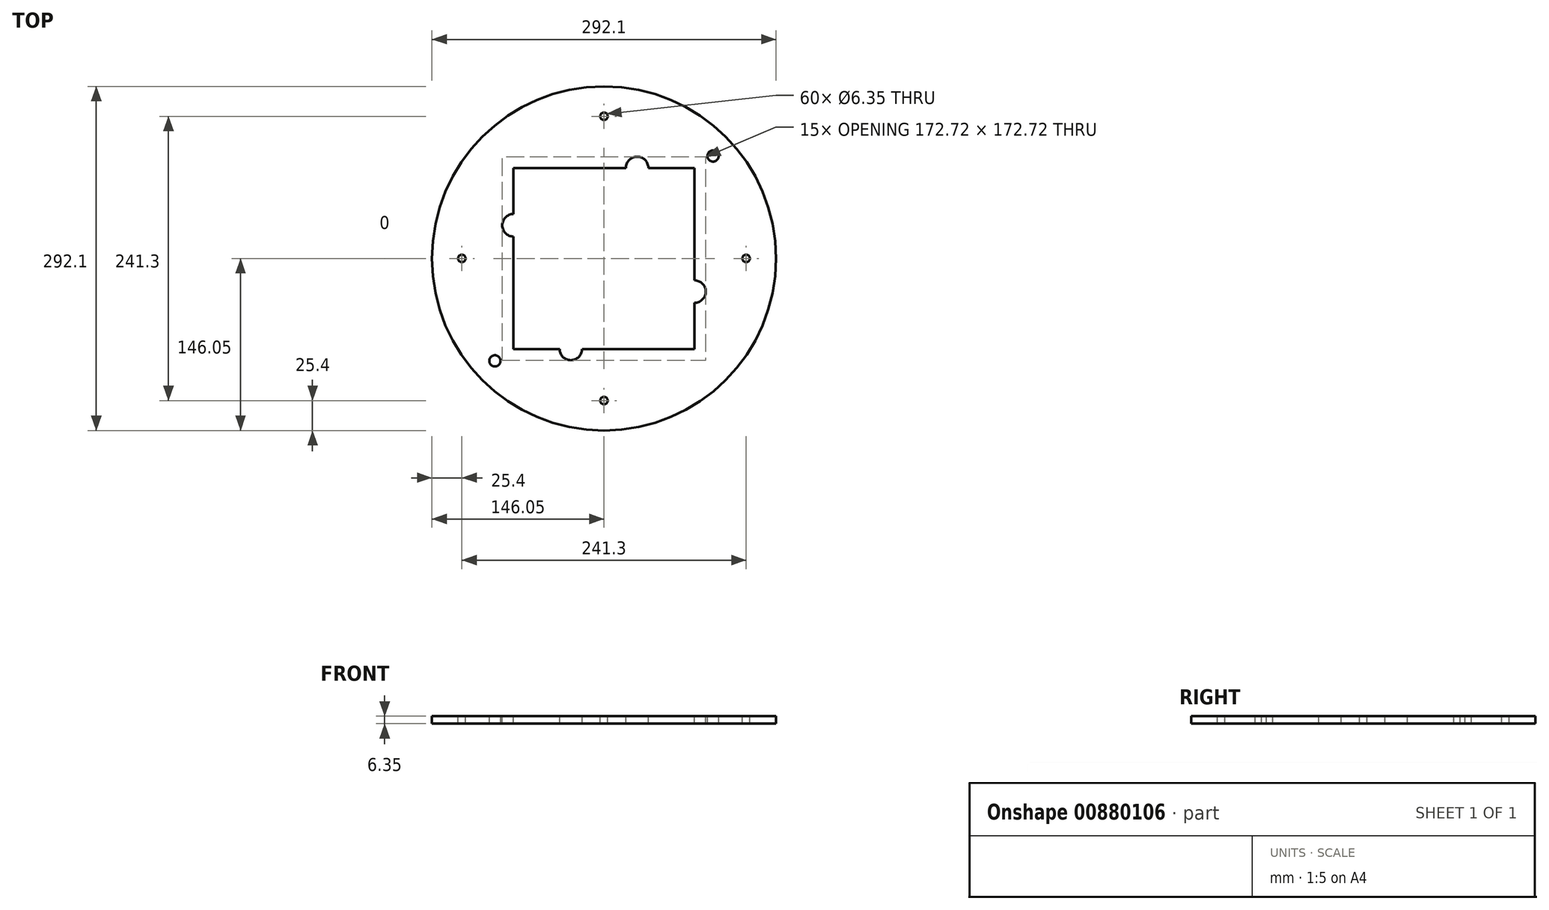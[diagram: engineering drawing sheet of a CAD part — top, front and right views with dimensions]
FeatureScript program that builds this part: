
annotation { "Feature Type Name" : "Feature", "Feature Type Description" : "" }
export const myFeature = defineFeature(function(context is Context, id is Id, definition is map)
    precondition{}
    {
        {
            var Q0;
            Q0=qCreatedBy(makeId("Top.planeOp"),FACE);
            var sketch = newSketch(context, id + "F0", { "sketchPlane" : qUnion([Q0])});
            skCircle(sketch, "E0", {"center": v(0, 0) * mm, "radius": 146.05 * mm});
            skSolve(sketch);
        }
        {
            var Q0;
            Q0=makeQuery(id+"F0.imprint","IMPRINT",FACE,{"disambiguationData":[TD([[makeQuery(id+"F0.imprint","IMPRINT",EDGE,{"derivedFrom":sQuery(id+"F0.wireOp",EDGE,"E0")}),1.0]])]});
            extrude(context, id + "F1", {"entities" : qUnion([Q0]), "depth" : 6.35 * mm, "offsetDistance" : 25.4 * mm});
        }
        {
            var Q0;
            Q0=makeQuery(id+"F1.opExtrude","CAP_FACE",FACE,{"disambiguationData":[OSD([sQuery(id+"F0.wireOp",EDGE,"E0")])],"isStart":false});
            var sketch = newSketch(context, id + "F2", { "sketchPlane" : qUnion([Q0])});
            skCircle(sketch, "E1", {"center": v(120.65, 0) * mm, "radius": 3.18 * mm});
            skCircle(sketch, "E2.1.0", {"center": v(0, 120.65) * mm, "radius": 3.18 * mm});
            skCircle(sketch, "E2.2.0", {"center": v(-120.65, 0) * mm, "radius": 3.18 * mm});
            skCircle(sketch, "E2.3.0", {"center": v(0, -120.65) * mm, "radius": 3.18 * mm});
            skPoint(sketch, "E2.center", {"position": v(0, 0) * mm});
            skCircle(sketch, "E3", {"center": v(92.59, 86.93) * mm, "radius": 4.76 * mm});
            skCircle(sketch, "E4.1.0", {"center": v(-92.59, -86.93) * mm, "radius": 4.76 * mm});
            skSolve(sketch);
        }
        {
            var Q0;
            Q0=sQuery(id+"F2.wireOp",VERTEX,"E1.center");
            var Q1;
            Q1=sQuery(id+"F2.wireOp",VERTEX,"E2.3.0.center");
            var Q2;
            Q2=sQuery(id+"F2.wireOp",VERTEX,"E2.2.0.center");
            var Q3;
            Q3=sQuery(id+"F2.wireOp",VERTEX,"E2.1.0.center");
            var Q4;
            Q4=makeQuery(id+"F1.opExtrude","SWEPT_BODY",BODY,{"disambiguationData":[OSD([sQuery(id+"F0.wireOp",EDGE,"E0")])]});
            hole(context, id + "F3", {"style" : HoleStyle.SIMPLE, "endStyle" : HoleEndStyle.THROUGH, "holeDiameter" : 6.35 * mm, "majorDiameter" : 6.35 * mm, "isTappedThrough" : true, "tappedDepth" : 12.7 * mm, "tapClearance" : 3, "locations" : qUnion([Q0, Q1, Q2, Q3]), "scope" : qUnion([Q4])});
        }
        {
            var Q0;
            Q0=sQuery(id+"F2.wireOp",VERTEX,"E4.1.0.center");
            var Q1;
            Q1=sQuery(id+"F2.wireOp",VERTEX,"E3.center");
            var Q2;
            Q2=makeQuery(id+"F1.opExtrude","SWEPT_BODY",BODY,{"disambiguationData":[OSD([sQuery(id+"F0.wireOp",EDGE,"E0")])]});
            hole(context, id + "F4", {"style" : HoleStyle.SIMPLE, "endStyle" : HoleEndStyle.THROUGH, "holeDiameter" : 9.52 * mm, "majorDiameter" : 6.35 * mm, "isTappedThrough" : true, "tappedDepth" : 12.7 * mm, "tapClearance" : 3, "locations" : qUnion([Q0, Q1]), "scope" : qUnion([Q2])});
        }
        {
            var Q0;
            Q0=makeQuery(id+"F1.opExtrude","CAP_FACE",FACE,{"disambiguationData":[OSD([sQuery(id+"F0.wireOp",EDGE,"E0")])],"isStart":false});
            var sketch = newSketch(context, id + "F5", { "sketchPlane" : qUnion([Q0])});
            skLineSegment(sketch, "E5.0", {"start": v(76.83, 76.84) * mm, "end": v(76.83, -18.62) * mm});
            skLineSegment(sketch, "E5.1", {"start": v(76.84, -76.83) * mm, "end": v(-18.62, -76.83) * mm});
            skLineSegment(sketch, "E5.2", {"start": v(-76.83, -76.84) * mm, "end": v(-76.83, 18.62) * mm});
            skLineSegment(sketch, "E5.3", {"start": v(-76.84, 76.83) * mm, "end": v(18.62, 76.83) * mm});
            skArc(sketch, "E6", {"start": v(76.84, -37.67) * mm, "mid": v(86.36, -28.15) * mm, "end": v(76.83, -18.62) * mm});
            skArc(sketch, "E7.1.0", {"start": v(37.67, 76.84) * mm, "mid": v(28.15, 86.36) * mm, "end": v(18.62, 76.83) * mm});
            skArc(sketch, "E7.2.0", {"start": v(-76.84, 37.67) * mm, "mid": v(-86.36, 28.15) * mm, "end": v(-76.83, 18.62) * mm});
            skArc(sketch, "E7.3.0", {"start": v(-37.67, -76.84) * mm, "mid": v(-28.15, -86.36) * mm, "end": v(-18.62, -76.83) * mm});
            skLineSegment(sketch, "E8.trimOffspring", {"start": v(-76.84, 37.67) * mm, "end": v(-76.84, 76.83) * mm});
            skLineSegment(sketch, "E9.trimOffspring", {"start": v(37.67, 76.84) * mm, "end": v(76.83, 76.84) * mm});
            skLineSegment(sketch, "E10.trimOffspring", {"start": v(76.84, -37.67) * mm, "end": v(76.84, -76.83) * mm});
            skLineSegment(sketch, "E11.trimOffspring", {"start": v(-37.67, -76.84) * mm, "end": v(-76.83, -76.84) * mm});
            skSolve(sketch);
        }
        {
            var Q0;
            Q0=qSketchRegion(id+"F5",true);
            extrude(context, id + "F6", {"entities" : qUnion([Q0]), "operationType" : NewBodyOperationType.REMOVE, "endBound" : BoundingType.THROUGH_ALL, "oppositeDirection" : true, "depth" : 25.4 * mm, "offsetDistance" : 25.4 * mm});
        }
    });
